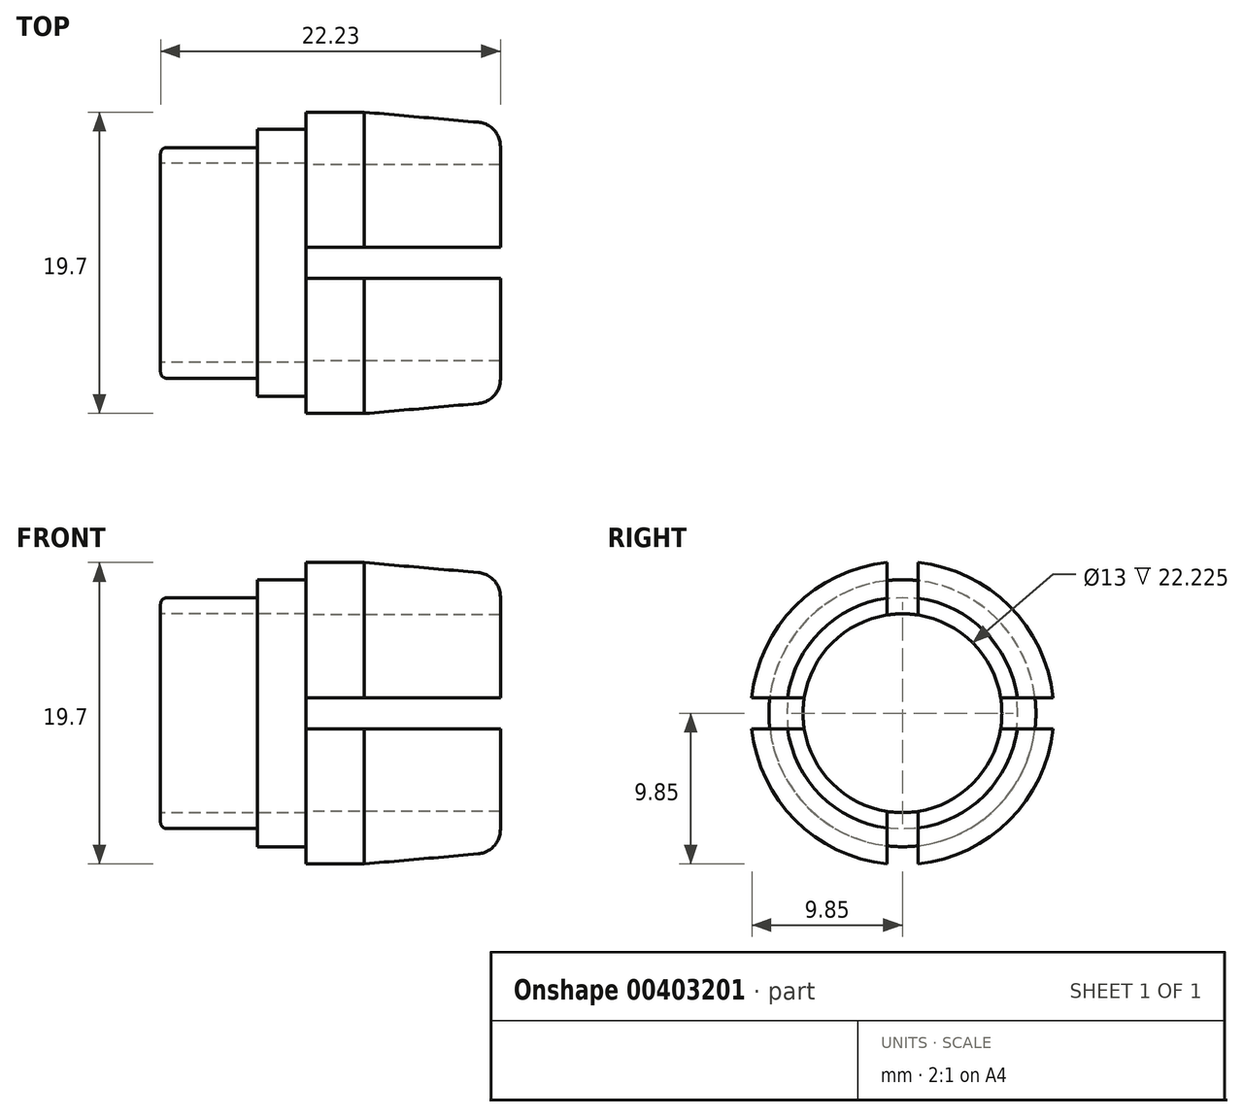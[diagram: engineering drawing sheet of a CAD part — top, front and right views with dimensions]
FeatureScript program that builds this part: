
annotation { "Feature Type Name" : "Feature", "Feature Type Description" : "" }
export const myFeature = defineFeature(function(context is Context, id is Id, definition is map)
    precondition{}
    {
        {
            var Q0;
            Q0=qCreatedBy(makeId("Front.planeOp"),FACE);
            var sketch = newSketch(context, id + "F0", { "sketchPlane" : qUnion([Q0])});
            skLineSegment(sketch, "E0", {"start": v(-22.22, 0) * mm, "end": v(21.75, 0) * mm, "construction": true});
            skLineSegment(sketch, "E1", {"start": v(6.93, 9.25) * mm, "end": v(-0.52, 9.9) * mm});
            skLineSegment(sketch, "E2", {"start": v(-0.52, 9.9) * mm, "end": v(-4.33, 9.9) * mm});
            skArc(sketch, "E3.filletArc", {"start": v(8.37, 7.59) * mm, "mid": v(7.99, 8.71) * mm, "end": v(6.93, 9.25) * mm});
            skLineSegment(sketch, "E4", {"start": v(-4.33, 9.9) * mm, "end": v(-4.33, 8.73) * mm});
            skLineSegment(sketch, "E5", {"start": v(-4.33, 8.73) * mm, "end": v(-7.5, 8.73) * mm});
            skLineSegment(sketch, "E6", {"start": v(-7.5, 8.73) * mm, "end": v(-7.5, 7.54) * mm});
            skLineSegment(sketch, "E7", {"start": v(-7.5, 7.54) * mm, "end": v(-13.45, 7.54) * mm});
            skLineSegment(sketch, "E8", {"start": v(-13.85, 6.5) * mm, "end": v(8.37, 6.5) * mm});
            skLineSegment(sketch, "E9", {"start": v(8.37, 7.59) * mm, "end": v(8.37, 6.5) * mm});
            skLineSegment(sketch, "E10", {"start": v(-13.85, 7.15) * mm, "end": v(-13.85, 6.5) * mm});
            skPoint(sketch, "E11.visualSharp", {"position": v(-13.85, 7.54) * mm});
            skArc(sketch, "E11.filletArc", {"start": v(-13.45, 7.54) * mm, "mid": v(-13.74, 7.43) * mm, "end": v(-13.85, 7.15) * mm});
            skSolve(sketch);
        }
        {
            var Q0;
            Q0=makeQuery(id+"F0.imprint","IMPRINT",FACE,{"disambiguationData":[TD([[makeQuery(id+"F0.imprint","IMPRINT",EDGE,{"derivedFrom":sQuery(id+"F0.wireOp",EDGE,"E1")}),1.0]])]});
            var Q1;
            Q1 = qSketchRegion(id + "F2", true);
            var Q2;
            Q2=sQuery(id+"F0.wireOp",EDGE,"E0");
            revolve(context, id + "F1", {"entities" : qUnion([Q0, Q1]), "axis" : qUnion([Q2]), "revolveType" : RevolveType.FULL});
        }
        {
            var Q0;
            Q0=qCreatedBy(makeId("Right.planeOp"),FACE);
            var sketch = newSketch(context, id + "F2", { "sketchPlane" : qUnion([Q0])});
            skCircle(sketch, "E12", {"center": v(0, 0) * mm, "radius": 8.53 * mm, "construction": true});
            skPoint(sketch, "E13", {"position": v(0, -8.53) * mm});
            skPoint(sketch, "E14", {"position": v(8.53, 0) * mm});
            skLineSegment(sketch, "E15", {"start": v(1.02, -9.93) * mm, "end": v(-1.02, -9.93) * mm});
            skLineSegment(sketch, "E16", {"start": v(-1.02, -9.93) * mm, "end": v(-1.02, -6.38) * mm});
            skLineSegment(sketch, "E17", {"start": v(-1.02, -6.38) * mm, "end": v(1.02, -6.38) * mm});
            skLineSegment(sketch, "E18", {"start": v(1.02, -6.38) * mm, "end": v(1.02, -9.93) * mm});
            skPoint(sketch, "E19", {"position": v(0, 8.53) * mm});
            skLineSegment(sketch, "E20", {"start": v(1.02, 6.38) * mm, "end": v(-1.02, 6.38) * mm});
            skLineSegment(sketch, "E21", {"start": v(-1.02, 6.38) * mm, "end": v(-1.02, 9.93) * mm});
            skLineSegment(sketch, "E22", {"start": v(-1.02, 9.93) * mm, "end": v(1.02, 9.93) * mm});
            skLineSegment(sketch, "E23", {"start": v(1.02, 9.93) * mm, "end": v(1.02, 6.38) * mm});
            skLineSegment(sketch, "E24", {"start": v(-9.93, -1.02) * mm, "end": v(-9.93, 1.02) * mm});
            skLineSegment(sketch, "E25", {"start": v(-9.93, 1.02) * mm, "end": v(-6.38, 1.02) * mm});
            skLineSegment(sketch, "E26", {"start": v(-6.38, 1.02) * mm, "end": v(-6.38, -1.02) * mm});
            skLineSegment(sketch, "E27", {"start": v(-6.38, -1.02) * mm, "end": v(-9.93, -1.02) * mm});
            skLineSegment(sketch, "E28", {"start": v(-10.98, 0) * mm, "end": v(11.1, 0) * mm, "construction": true});
            skLineSegment(sketch, "E29", {"start": v(6.38, -1.02) * mm, "end": v(6.38, 1.02) * mm});
            skLineSegment(sketch, "E30", {"start": v(6.38, 1.02) * mm, "end": v(9.93, 1.02) * mm});
            skLineSegment(sketch, "E31", {"start": v(9.93, 1.02) * mm, "end": v(9.93, -1.02) * mm});
            skLineSegment(sketch, "E32", {"start": v(9.93, -1.02) * mm, "end": v(6.38, -1.02) * mm});
            skSolve(sketch);
        }
        {
            var Q0;
            Q0 = qSketchRegion(id + "F2", true);
            extrude(context, id + "F3", {"entities" : qUnion([Q0]), "operationType" : NewBodyOperationType.REMOVE, "depth" : 25.4 * mm, "hasSecondDirection" : true, "secondDirectionOppositeDirection" : true, "secondDirectionDepth" : 4.34 * mm});
        }
    });
